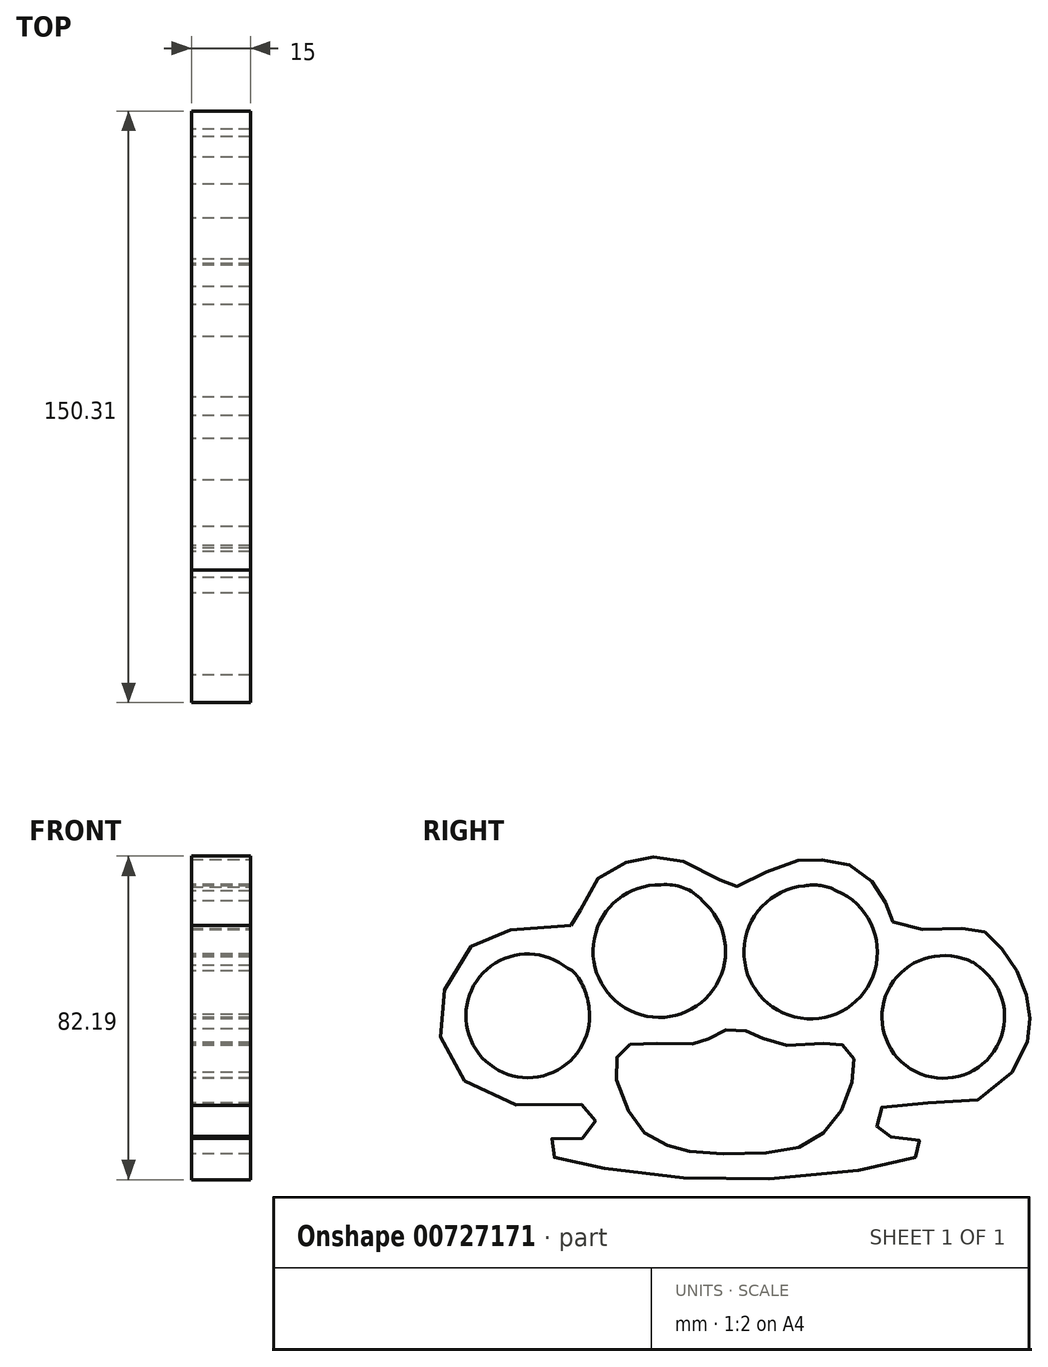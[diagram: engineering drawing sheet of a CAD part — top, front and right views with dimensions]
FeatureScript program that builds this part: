
annotation { "Feature Type Name" : "Feature", "Feature Type Description" : "" }
export const myFeature = defineFeature(function(context is Context, id is Id, definition is map)
    precondition{}
    {
        {
            var Q0;
            Q0=qCreatedBy(makeId("Right.planeOp"),FACE);
            var sketch = newSketch(context, id + "F0", { "sketchPlane" : qUnion([Q0])});
            skFitSpline(sketch, "E0", {"points": [v(-42, 37.36) * mm, v(-59.24, 35.94) * mm, v(-67.01, 32.43) * mm, v(-73.81, 21.9) * mm, v(-75.6, 10.9) * mm, v(-70.78, 0) * mm, v(-59.05, -7.94) * mm, v(-38.85, -8.25) * mm, v(-36.86, -9.61) * mm, v(-35.92, -11.92) * mm, v(-36.48, -14.92) * mm, v(-38.35, -16.54) * mm, v(-40.97, -16.66) * mm, v(-46.57, -16.66) * mm, v(-47.81, -18.78) * mm, v(-47.44, -20.77) * mm, v(-43.45, -22.51) * mm, v(-20.85, -26.12) * mm, v(14.9, -26.74) * mm, v(43.56, -22.39) * mm, v(46.8, -20.52) * mm, v(47.3, -18.53) * mm, v(46.17, -17.04) * mm, v(43.93, -16.66) * mm, v(38.2, -16.29) * mm, v(37.09, -15.67) * mm, v(36.1, -14.8) * mm, v(35.47, -12.93) * mm, v(35.6, -10.69) * mm, v(36.84, -8.94) * mm, v(38.46, -7.95) * mm, v(58.5, -7.85) * mm, v(62.02, -6.53) * mm, v(69.9, 0) * mm], "startDerivative": vector(-379.65, -57) * mm, "endDerivative": vector(227.63, 261.8) * mm});
            skFitSpline(sketch, "E1", {"points": [v(-42, 37.36) * mm, v(-40.82, 38.53) * mm, v(-34.82, 49.73) * mm, v(-24.45, 54.08) * mm, v(-15.87, 54.42) * mm, v(-1.66, 47.42) * mm, v(0, 47.22) * mm, v(12.34, 52.92) * mm, v(19.87, 54) * mm, v(28.47, 52.73) * mm, v(35.4, 47.4) * mm, v(38.39, 41.42) * mm, v(40.83, 37.36) * mm, v(56.75, 36.5) * mm, v(63.23, 35.54) * mm, v(68.03, 30.63) * mm, v(72.33, 23.48) * mm, v(74.25, 16.63) * mm, v(74.4, 10.2) * mm, v(69.9, 0) * mm], "startDerivative": vector(46.68, 27.06) * mm, "endDerivative": vector(-153.52, -232.13) * mm});
            skArc(sketch, "E2", {"start": v(-43.99, 27.2) * mm, "mid": v(-66.9, 6.97) * mm, "end": v(-37.32, 14.65) * mm});
            skArc(sketch, "E3", {"start": v(-19.16, 47.6) * mm, "mid": v(-25.62, 15.05) * mm, "end": v(-8.7, 43.6) * mm});
            skArc(sketch, "E4", {"start": v(17.26, 47.39) * mm, "mid": v(16.26, 13.76) * mm, "end": v(25.4, 46.14) * mm});
            skArc(sketch, "E5", {"start": v(55.98, 29.25) * mm, "mid": v(45.44, 0.18) * mm, "end": v(62.85, 25.74) * mm});
            skFitSpline(sketch, "E6", {"points": [v(-11.14, 7.15) * mm, v(-24.06, 7.4) * mm, v(-27.94, 6.67) * mm, v(-30.42, 3.78) * mm, v(-30.7, -1.32) * mm, v(-26.48, -11.56) * mm, v(-22, -16.5) * mm, v(-15.48, -19.28) * mm, v(-9.87, -20.34) * mm, v(7, -20.54) * mm, v(17.62, -18.36) * mm, v(24.26, -13.22) * mm, v(28.62, -5.28) * mm, v(29.92, 2.06) * mm, v(29.07, 5.04) * mm, v(26.16, 7.32) * mm, v(22.32, 7.36) * mm, v(9.58, 7.2) * mm, v(5.85, 9.17) * mm, v(2.38, 10.53) * mm, v(-1.84, 10.9) * mm, v(-4.94, 9.62) * mm, v(-8.88, 7.73) * mm, v(-11.14, 7.15) * mm]});
            skFitSpline(sketch, "E7", {"points": [v(-43.99, 27.2) * mm, v(-41.2, 25.31) * mm, v(-38.36, 20.25) * mm, v(-37.32, 14.65) * mm], "startDerivative": vector(7.83, -6.02) * mm, "endDerivative": vector(1.1, -16.43) * mm});
            skArc(sketch, "E8", {"start": v(-8.7, 43.6) * mm, "mid": v(-13.44, 46.87) * mm, "end": v(-19.16, 47.6) * mm});
            skArc(sketch, "E9", {"start": v(25.4, 46.14) * mm, "mid": v(21.43, 47.43) * mm, "end": v(17.26, 47.39) * mm});
            skArc(sketch, "E10", {"start": v(62.85, 25.74) * mm, "mid": v(59.72, 28.09) * mm, "end": v(55.98, 29.25) * mm});
            skSolve(sketch);
        }
        {
            var Q0;
            Q0=makeQuery(id+"F0.imprint","IMPRINT",FACE,{"disambiguationData":[TD([[makeQuery(id+"F0.imprint","IMPRINT",EDGE,{"derivedFrom":sQuery(id+"F0.wireOp",EDGE,"E0")}),1.0]])]});
            extrude(context, id + "F1", {"entities" : qUnion([Q0]), "depth" : 15 * mm, "offsetDistance" : 25 * mm, "symmetric" : true});
        }
    });
